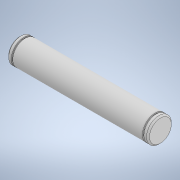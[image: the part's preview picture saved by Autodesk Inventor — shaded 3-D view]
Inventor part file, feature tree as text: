
AUTODESK INVENTOR PART (.ipt)
format: ipt  version: 2022 (Build 260153000, 153)  size: 125,952 bytes
history: native  units: mm
features: revolve x1, sketch x1
ambient origin geometry x8: Origin, YZ Plane, XZ Plane, XY Plane, X Axis, Y Axis, Z Axis, Center Point
bodies: Solid1 (feature_tree)
feature tree (2):
  revolve  "Revolution1"  [1 undecoded]
  sketch  "Sketch1"  dims[d0=6.0mm d1=0.7mm d2=2.0mm d3=0.5mm d4=135.0deg d5=1.0mm d7=90.0deg d8=31.5mm]
note: 1 required parameter value undecoded (feature->parameter linkage not recoverable at this tier; creation-order binding heuristic only, values carry confidence <= 0.55)
